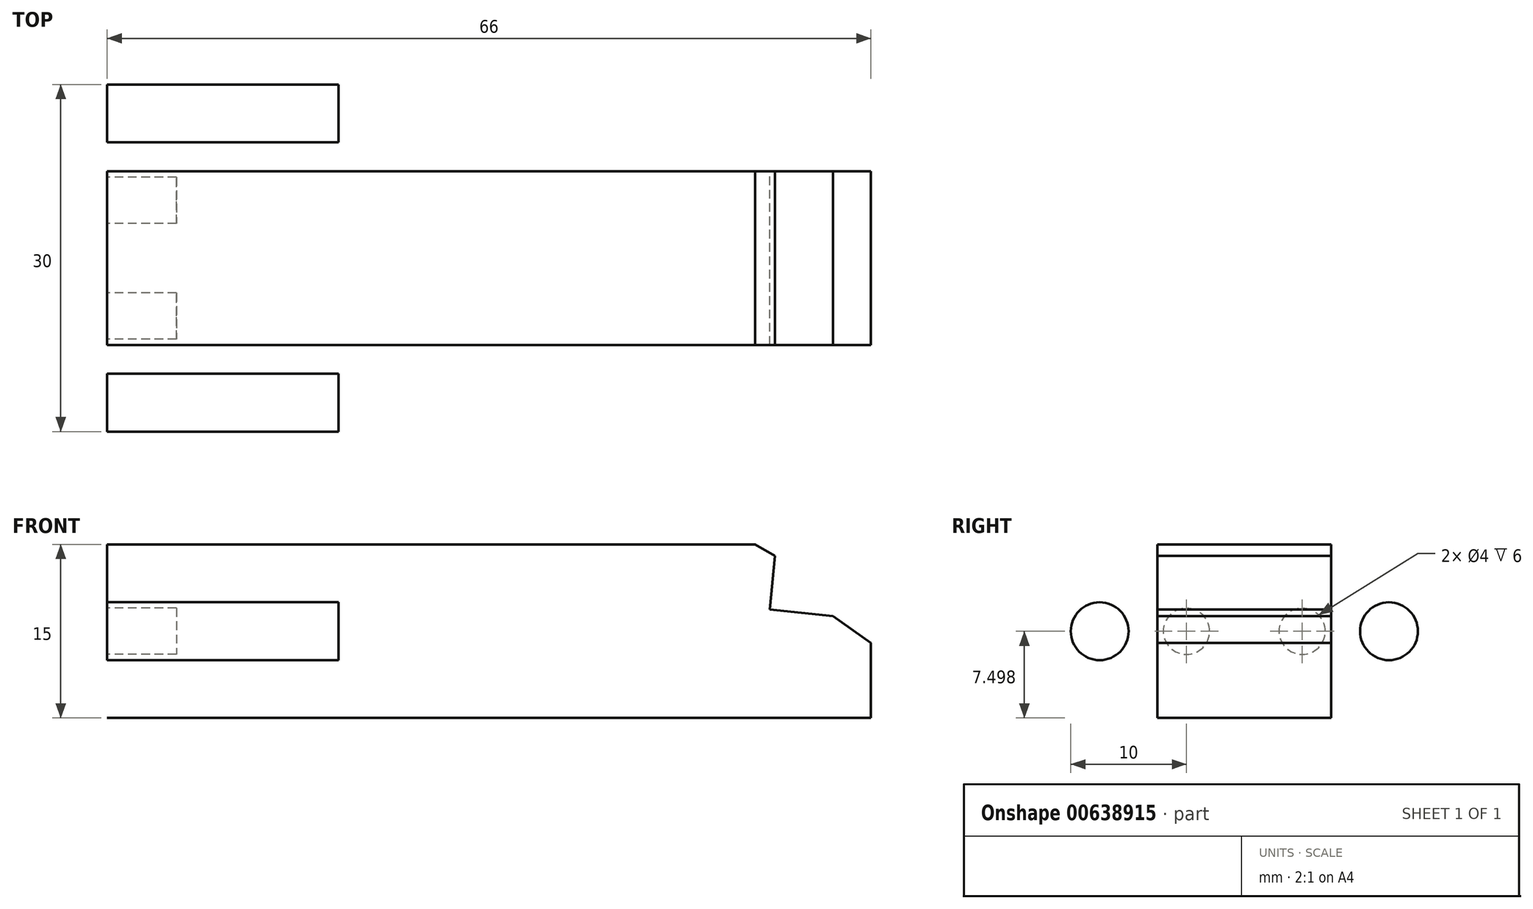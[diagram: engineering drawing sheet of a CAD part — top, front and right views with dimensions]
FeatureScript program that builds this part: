
annotation { "Feature Type Name" : "Feature", "Feature Type Description" : "" }
export const myFeature = defineFeature(function(context is Context, id is Id, definition is map)
    precondition{}
    {
        {
            var Q0;
            Q0=qCreatedBy(makeId("Front.planeOp"),FACE);
            var sketch = newSketch(context, id + "F0", { "sketchPlane" : qUnion([Q0])});
            skLineSegment(sketch, "E0", {"start": v(79.63, -49.67) * mm, "end": v(79.63, -34.67) * mm});
            skLineSegment(sketch, "E1", {"start": v(69.63, -49.67) * mm, "end": v(69.63, -34.67) * mm});
            skLineSegment(sketch, "E2", {"start": v(54.63, -49.67) * mm, "end": v(54.63, -34.67) * mm});
            skLineSegment(sketch, "E3", {"start": v(44.63, -49.67) * mm, "end": v(44.63, -34.67) * mm});
            skLineSegment(sketch, "E4", {"start": v(54.63, -40.85) * mm, "end": v(69.63, -40.85) * mm});
            skCircle(sketch, "E5", {"center": v(67.13, -42.17) * mm, "radius": 2 * mm});
            skCircle(sketch, "E6", {"center": v(74.63, -42.17) * mm, "radius": 2.5 * mm});
            skCircle(sketch, "E7", {"center": v(49.63, -42.17) * mm, "radius": 2.5 * mm});
            skLineSegment(sketch, "E8", {"start": v(79.63, -49.67) * mm, "end": v(44.63, -49.67) * mm});
            skLineSegment(sketch, "E9", {"start": v(79.63, -34.67) * mm, "end": v(44.63, -34.67) * mm});
            skLineSegment(sketch, "E10", {"start": v(54.63, -43.17) * mm, "end": v(69.63, -43.17) * mm});
            skLineSegment(sketch, "E11", {"start": v(54.63, -40.3) * mm, "end": v(69.63, -40.3) * mm});
            skLineSegment(sketch, "E12", {"start": v(54.63, -35.67) * mm, "end": v(69.63, -35.67) * mm});
            skCircle(sketch, "E13", {"center": v(57.13, -42.17) * mm, "radius": 2 * mm});
            skLineSegment(sketch, "E14", {"start": v(-11.63, -43.18) * mm, "end": v(-11.63, -49.67) * mm});
            skLineSegment(sketch, "E15", {"start": v(-57.63, -34.67) * mm, "end": v(-57.63, -49.67) * mm});
            skLineSegment(sketch, "E16", {"start": v(-77.63, -34.67) * mm, "end": v(-77.63, -49.67) * mm});
            skLineSegment(sketch, "E17", {"start": v(-11.63, -49.67) * mm, "end": v(-77.63, -49.67) * mm});
            skLineSegment(sketch, "E18", {"start": v(-21.63, -34.67) * mm, "end": v(-77.63, -34.67) * mm});
            skLineSegment(sketch, "E19", {"start": v(-14.88, -40.85) * mm, "end": v(-20.37, -40.3) * mm});
            skLineSegment(sketch, "E20", {"start": v(-79.63, -42.17) * mm, "end": v(-55.63, -42.17) * mm});
            skLineSegment(sketch, "E21", {"start": v(-11.63, -43.18) * mm, "end": v(-14.88, -40.85) * mm});
            skLineSegment(sketch, "E22", {"start": v(-20.37, -40.3) * mm, "end": v(-19.91, -35.67) * mm});
            skLineSegment(sketch, "E23", {"start": v(-19.91, -35.67) * mm, "end": v(-21.63, -34.67) * mm});
            skLineSegment(sketch, "E24", {"start": v(-11.63, 39.67) * mm, "end": v(-11.63, 24.67) * mm});
            skLineSegment(sketch, "E25", {"start": v(-77.63, 49.67) * mm, "end": v(-77.63, 14.67) * mm});
            skLineSegment(sketch, "E26", {"start": v(-57.63, 49.67) * mm, "end": v(-57.63, 39.67) * mm});
            skLineSegment(sketch, "E27", {"start": v(-57.63, 14.67) * mm, "end": v(-77.63, 14.67) * mm});
            skLineSegment(sketch, "E28", {"start": v(-11.63, 24.67) * mm, "end": v(-57.63, 24.67) * mm});
            skLineSegment(sketch, "E29", {"start": v(-11.63, 39.67) * mm, "end": v(-57.63, 39.67) * mm});
            skLineSegment(sketch, "E30", {"start": v(-57.63, 49.67) * mm, "end": v(-77.63, 49.67) * mm});
            skLineSegment(sketch, "E31", {"start": v(-57.63, 24.67) * mm, "end": v(-57.63, 14.67) * mm});
            skSolve(sketch);
        }
        {
            var Q0;
            {var subQ0=sQuery(id+"F0.wireOp",EDGE,"E17");var subQ1=sQuery(id+"F0.wireOp",EDGE,"E15");var subQ2=makeQuery(id+"F0.imprint","INTERSECT",VERTEX,{"derivedFrom":[subQ1,subQ0]});Q0=makeQuery(id+"F0.imprint","IMPRINT",FACE,{"disambiguationData":[TD([[makeQuery(id+"F0.imprint","IMPRINT",EDGE,{"disambiguationData":[TD([[subQ2,1.0]])],"derivedFrom":subQ1}),-1.0]])]});}
            var Q1;
            {var subQ0=sQuery(id+"F0.wireOp",EDGE,"E18");var subQ1=sQuery(id+"F0.wireOp",EDGE,"E15");var subQ2=makeQuery(id+"F0.imprint","INTERSECT",VERTEX,{"derivedFrom":[subQ1,subQ0]});Q1=makeQuery(id+"F0.imprint","IMPRINT",FACE,{"disambiguationData":[TD([[makeQuery(id+"F0.imprint","IMPRINT",EDGE,{"disambiguationData":[TD([[subQ2,-1.0]])],"derivedFrom":subQ1}),-1.0]])]});}
            var Q2;
            {var subQ7=sQuery(id+"F0.wireOp",EDGE,"E14");Q2=makeQuery(id+"F0.imprint","IMPRINT",FACE,{"disambiguationData":[TD([[makeQuery(id+"F0.imprint","IMPRINT",EDGE,{"derivedFrom":subQ7}),-1.0]])]});}
            extrude(context, id + "F1", {"entities" : qUnion([Q0, Q1, Q2]), "depth" : 35 * mm, "offsetDistance" : 25 * mm});
        }
        {
            var Q0;
            Q0=makeQuery(id+"F1.opExtrude","SWEPT_FACE",FACE,{"disambiguationData":[OSD([sQuery(id+"F0.wireOp",EDGE,"E18")])]});
            var sketch = newSketch(context, id + "F2", { "sketchPlane" : qUnion([Q0])});
            skLineSegment(sketch, "E32.0", {"start": v(-77.63, -35) * mm, "end": v(-77.63, 0) * mm});
            skLineSegment(sketch, "E33.0", {"start": v(-21.63, 0) * mm, "end": v(-77.63, 0) * mm});
            skLineSegment(sketch, "E34.0", {"start": v(-21.63, -35) * mm, "end": v(-77.63, -35) * mm});
            skLineSegment(sketch, "E35.0", {"start": v(-11.63, 0) * mm, "end": v(-77.63, 0) * mm});
            skLineSegment(sketch, "E36.0", {"start": v(-11.63, -35) * mm, "end": v(-77.63, -35) * mm});
            skLineSegment(sketch, "E37.0", {"start": v(-11.63, -35) * mm, "end": v(-11.63, 0) * mm});
            skLineSegment(sketch, "E38", {"start": v(-11.63, -10) * mm, "end": v(-11.63, -25) * mm});
            skLineSegment(sketch, "E39", {"start": v(-77.63, 0) * mm, "end": v(-77.63, -35) * mm});
            skLineSegment(sketch, "E40", {"start": v(-57.63, 0) * mm, "end": v(-57.63, -10) * mm});
            skLineSegment(sketch, "E41", {"start": v(-57.63, -35) * mm, "end": v(-77.63, -35) * mm});
            skLineSegment(sketch, "E42", {"start": v(-11.63, -25) * mm, "end": v(-57.63, -25) * mm});
            skLineSegment(sketch, "E43", {"start": v(-11.63, -10) * mm, "end": v(-57.63, -10) * mm});
            skLineSegment(sketch, "E44", {"start": v(-57.63, 0) * mm, "end": v(-77.63, 0) * mm});
            skLineSegment(sketch, "E45", {"start": v(-57.63, -25) * mm, "end": v(-57.63, -35) * mm});
            skSolve(sketch);
        }
        {
            var Q0;
            {var subQ3=sQuery(id+"F2.wireOp",EDGE,"E40");Q0=makeQuery(id+"F2.imprint","IMPRINT",FACE,{"disambiguationData":[TD([[makeQuery(id+"F2.imprint","IMPRINT",EDGE,{"derivedFrom":subQ3}),1.0]])]});}
            var Q1;
            {var subQ0=sQuery(id+"F2.wireOp",EDGE,"E36.0");var subQ3=sQuery(id+"F2.wireOp",EDGE,"E37.0");var subQ4=makeQuery(id+"F2.imprint","INTERSECT",VERTEX,{"derivedFrom":[subQ0,subQ3]});Q1=makeQuery(id+"F2.imprint","IMPRINT",FACE,{"disambiguationData":[TD([[makeQuery(id+"F2.imprint","IMPRINT",EDGE,{"disambiguationData":[TD([[subQ4,-1.0]])],"derivedFrom":subQ0}),-1.0]])]});}
            var Q2;
            {var subQ0=sQuery(id+"F2.wireOp",EDGE,"E35.0");var subQ3=sQuery(id+"F2.wireOp",EDGE,"E37.0");var subQ4=makeQuery(id+"F2.imprint","INTERSECT",VERTEX,{"derivedFrom":[subQ0,subQ3]});Q2=makeQuery(id+"F2.imprint","IMPRINT",FACE,{"disambiguationData":[TD([[makeQuery(id+"F2.imprint","IMPRINT",EDGE,{"disambiguationData":[TD([[subQ4,-1.0]])],"derivedFrom":subQ0}),1.0]])]});}
            var Q3;
            {var subQ3=sQuery(id+"F2.wireOp",EDGE,"E45");Q3=makeQuery(id+"F2.imprint","IMPRINT",FACE,{"disambiguationData":[TD([[makeQuery(id+"F2.imprint","IMPRINT",EDGE,{"derivedFrom":subQ3}),1.0]])]});}
            extrude(context, id + "F3", {"entities" : qUnion([Q0, Q1, Q2, Q3]), "operationType" : NewBodyOperationType.REMOVE, "endBound" : BoundingType.THROUGH_ALL, "oppositeDirection" : true, "depth" : 25 * mm, "offsetDistance" : 25 * mm});
        }
        {
            var Q0;
            Q0=makeQuery(id+"F3.boolean.opBoolean","COPY",FACE,{"derivedFrom":makeQuery(id+"F3.opExtrude","SWEPT_FACE",FACE,{"disambiguationData":[OSD([sQuery(id+"F2.wireOp",EDGE,"E40")])]})});
            var sketch = newSketch(context, id + "F4", { "sketchPlane" : qUnion([Q0])});
            skLineSegment(sketch, "E46.0", {"start": v(0, -34.67) * mm, "end": v(-10, -34.67) * mm});
            skLineSegment(sketch, "E47.0", {"start": v(0, -49.67) * mm, "end": v(0, -34.67) * mm});
            skLineSegment(sketch, "E48.0", {"start": v(-35, -34.67) * mm, "end": v(0, -34.67) * mm});
            skPoint(sketch, "E49.0", {"position": v(-35, -42.17) * mm});
            skLineSegment(sketch, "E50.0", {"start": v(-35, -34.67) * mm, "end": v(-35, -49.67) * mm});
            skLineSegment(sketch, "E51.0.0", {"start": v(0, -34.67) * mm, "end": v(0, -49.67) * mm});
            skLineSegment(sketch, "E51.0.1", {"start": v(0, -49.67) * mm, "end": v(-35, -49.67) * mm});
            skLineSegment(sketch, "E51.0.2", {"start": v(-35, -49.67) * mm, "end": v(-35, -34.67) * mm});
            skPoint(sketch, "E52.0", {"position": v(0, -42.17) * mm});
            skLineSegment(sketch, "E53", {"start": v(-10, -49.67) * mm, "end": v(-10, -34.67) * mm});
            skLineSegment(sketch, "E54", {"start": v(-25, -49.67) * mm, "end": v(-25, -34.67) * mm});
            skLineSegment(sketch, "E55", {"start": v(-25, -40.85) * mm, "end": v(-10, -40.85) * mm});
            skCircle(sketch, "E56", {"center": v(-12.5, -42.17) * mm, "radius": 2 * mm});
            skCircle(sketch, "E57", {"center": v(-5, -42.17) * mm, "radius": 2.5 * mm});
            skCircle(sketch, "E58", {"center": v(-30, -42.17) * mm, "radius": 2.5 * mm});
            skLineSegment(sketch, "E59", {"start": v(0, -34.67) * mm, "end": v(-35, -34.67) * mm});
            skLineSegment(sketch, "E60", {"start": v(-25, -43.17) * mm, "end": v(-10, -43.17) * mm});
            skLineSegment(sketch, "E61", {"start": v(-25, -40.3) * mm, "end": v(-10, -40.3) * mm});
            skLineSegment(sketch, "E62", {"start": v(-25, -35.67) * mm, "end": v(-10, -35.67) * mm});
            skCircle(sketch, "E63", {"center": v(-22.5, -42.17) * mm, "radius": 2 * mm});
            skSolve(sketch);
        }
        {
            var Q0;
            Q0=makeQuery(id+"F4.imprint","IMPRINT",FACE,{"disambiguationData":[TD([[makeQuery(id+"F4.imprint","IMPRINT",EDGE,{"derivedFrom":sQuery(id+"F4.wireOp",EDGE,"E58")}),-1.0]])]});
            var Q1;
            Q1=makeQuery(id+"F4.imprint","IMPRINT",FACE,{"disambiguationData":[TD([[makeQuery(id+"F4.imprint","IMPRINT",EDGE,{"derivedFrom":sQuery(id+"F4.wireOp",EDGE,"E57")}),-1.0]])]});
            extrude(context, id + "F5", {"entities" : qUnion([Q0, Q1]), "operationType" : NewBodyOperationType.REMOVE, "endBound" : BoundingType.THROUGH_ALL, "oppositeDirection" : true, "depth" : 25 * mm, "offsetDistance" : 25 * mm});
        }
        {
            var Q0;
            Q0=makeQuery(id+"F1.opExtrude","SWEPT_FACE",FACE,{"disambiguationData":[OSD([sQuery(id+"F0.wireOp",EDGE,"E16")])]});
            var sketch = newSketch(context, id + "F6", { "sketchPlane" : qUnion([Q0])});
            skCircle(sketch, "E64.0", {"center": v(12.5, -42.17) * mm, "radius": 2 * mm});
            skCircle(sketch, "E65.0", {"center": v(22.5, -42.17) * mm, "radius": 2 * mm});
            skSolve(sketch);
        }
        {
            var Q0;
            Q0=makeQuery(id+"F6.imprint","IMPRINT",FACE,{"disambiguationData":[TD([[makeQuery(id+"F6.imprint","IMPRINT",EDGE,{"derivedFrom":sQuery(id+"F6.wireOp",EDGE,"E64.0")}),1.0]])]});
            var Q1;
            Q1=makeQuery(id+"F6.imprint","IMPRINT",FACE,{"disambiguationData":[TD([[makeQuery(id+"F6.imprint","IMPRINT",EDGE,{"derivedFrom":sQuery(id+"F6.wireOp",EDGE,"E65.0")}),1.0]])]});
            extrude(context, id + "F7", {"entities" : qUnion([Q0, Q1]), "operationType" : NewBodyOperationType.REMOVE, "oppositeDirection" : true, "depth" : 6 * mm, "offsetDistance" : 25 * mm});
        }
    });
